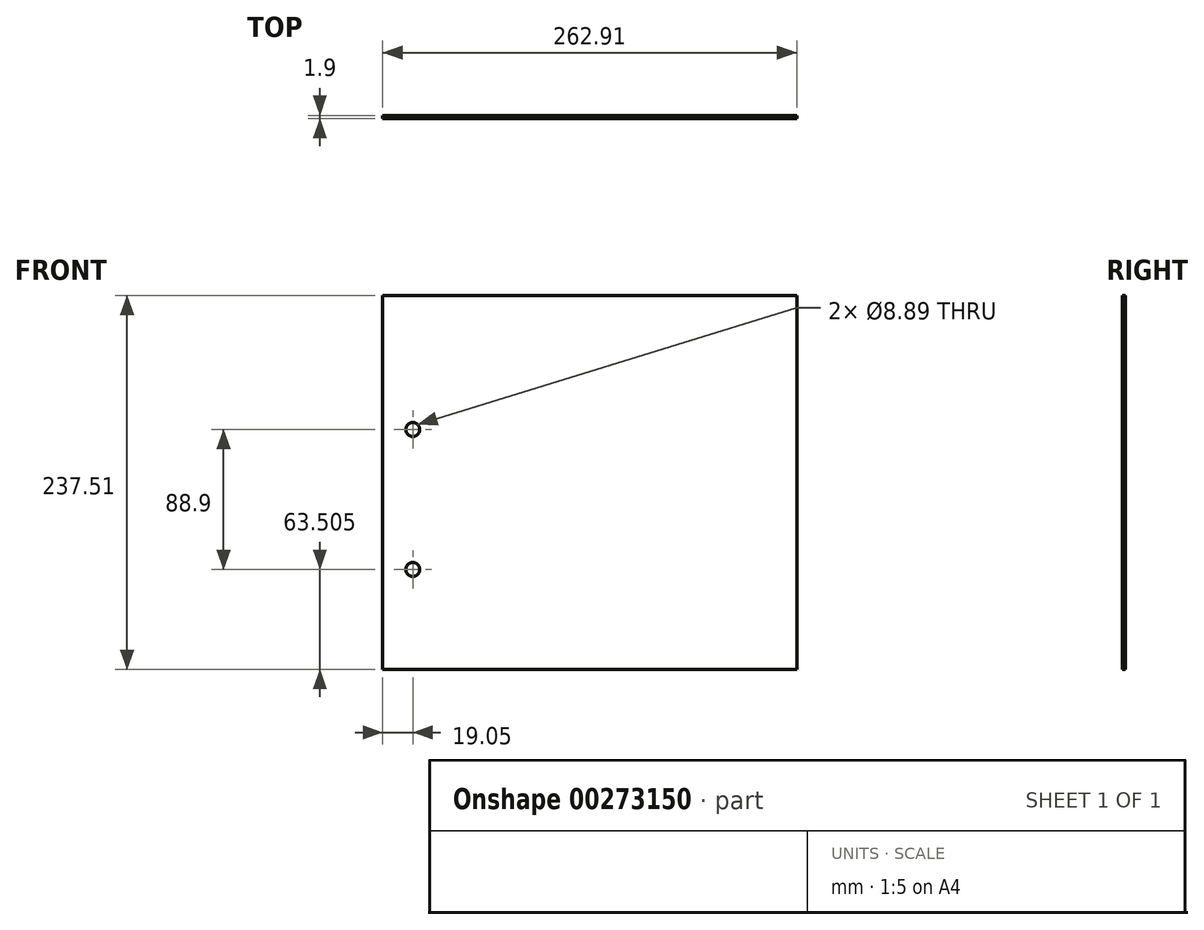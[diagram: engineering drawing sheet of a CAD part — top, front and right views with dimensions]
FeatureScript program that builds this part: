
annotation { "Feature Type Name" : "Feature", "Feature Type Description" : "" }
export const myFeature = defineFeature(function(context is Context, id is Id, definition is map)
    precondition{}
    {
        {
            var Q0;
            Q0=qCreatedBy(makeId("Front.planeOp"),FACE);
            var sketch = newSketch(context, id + "F0", { "sketchPlane" : qUnion([Q0])});
            skLineSegment(sketch, "E0.bottom", {"start": v(0, 0) * mm, "end": v(262.9, 0) * mm});
            skLineSegment(sketch, "E0.top", {"start": v(0, -237.5) * mm, "end": v(262.9, -237.5) * mm});
            skLineSegment(sketch, "E0.left", {"start": v(0, 0) * mm, "end": v(0, -237.5) * mm});
            skLineSegment(sketch, "E0.right", {"start": v(262.9, 0) * mm, "end": v(262.9, -237.5) * mm});
            skCircle(sketch, "E1", {"center": v(19.05, -85.1) * mm, "radius": 4.45 * mm});
            skCircle(sketch, "E2", {"center": v(19.05, -174) * mm, "radius": 4.45 * mm});
            skSolve(sketch);
        }
        {
            var Q0;
            Q0 = qSketchRegion(id + "F0", true);
            extrude(context, id + "F1", {"entities" : qUnion([Q0]), "depth" : 1.9 * mm});
        }
    });
